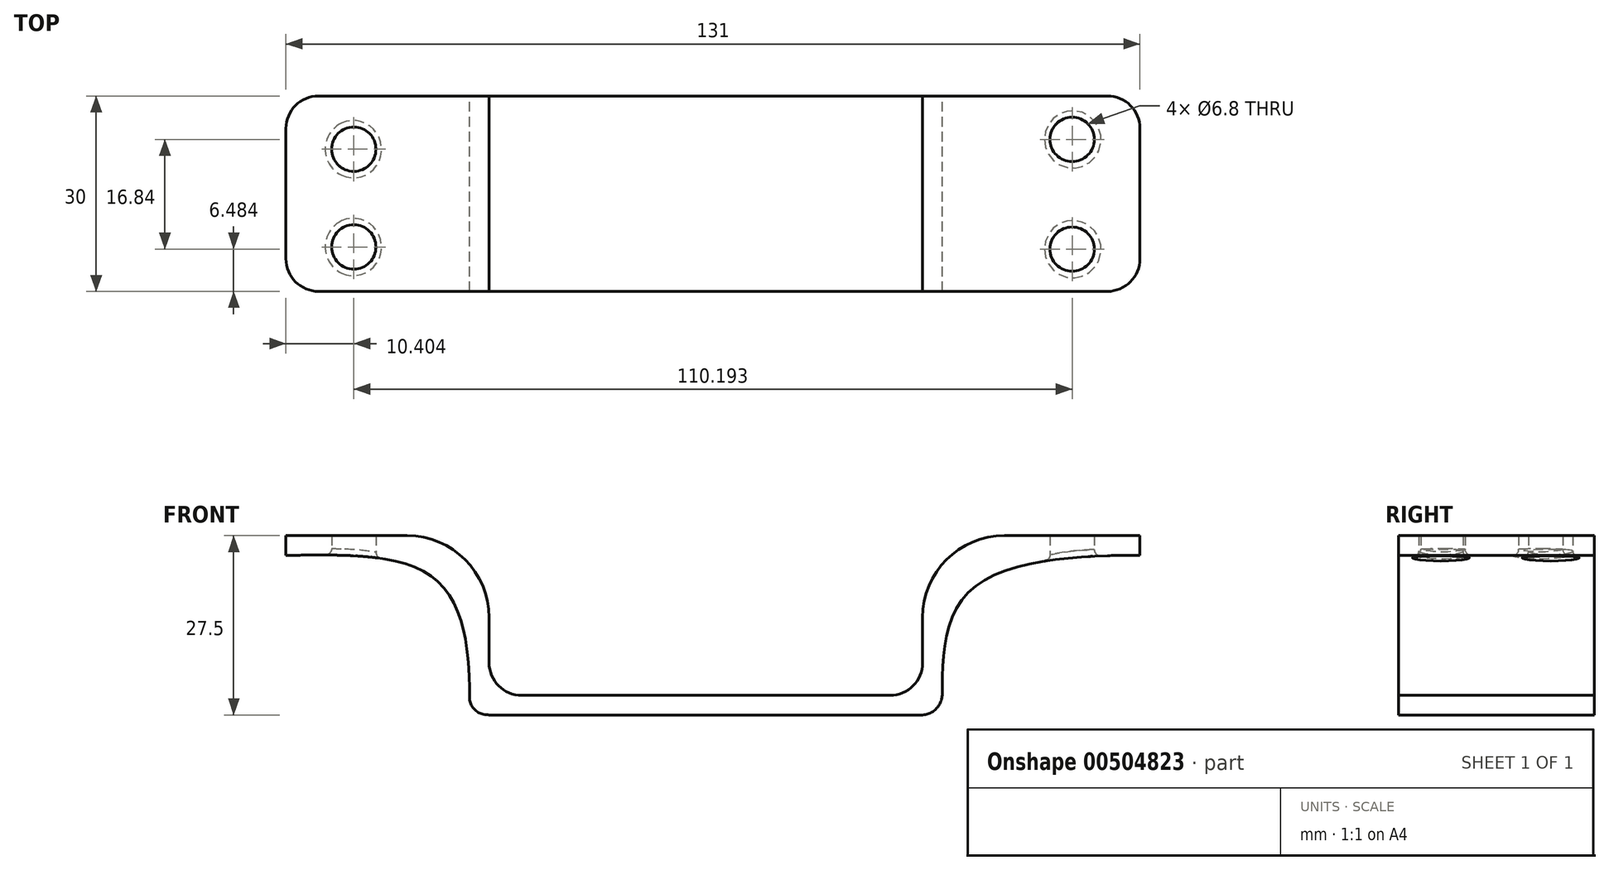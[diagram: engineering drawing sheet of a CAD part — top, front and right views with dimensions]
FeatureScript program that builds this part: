
annotation { "Feature Type Name" : "Feature", "Feature Type Description" : "" }
export const myFeature = defineFeature(function(context is Context, id is Id, definition is map)
    precondition{}
    {
        {
            var Q0;
            Q0=qCreatedBy(makeId("Front.planeOp"),FACE);
            var sketch = newSketch(context, id + "F0", { "sketchPlane" : qUnion([Q0])});
            skLineSegment(sketch, "E0.bottom", {"start": v(33.25, -1.5) * mm, "end": v(-33.25, -1.5) * mm});
            skLineSegment(sketch, "E0.top", {"start": v(33.25, 1.5) * mm, "end": v(-33.25, 1.5) * mm});
            skLineSegment(sketch, "E0.left", {"start": v(33.25, -1.5) * mm, "end": v(33.25, 1.5) * mm});
            skLineSegment(sketch, "E0.right", {"start": v(-33.25, -1.5) * mm, "end": v(-33.25, 1.5) * mm});
            skPoint(sketch, "E0.middle", {"position": v(0, 0) * mm});
            skLineSegment(sketch, "E1.bottom", {"start": v(33.25, 1.5) * mm, "end": v(36.25, 1.5) * mm});
            skLineSegment(sketch, "E1.top", {"start": v(33.25, 26) * mm, "end": v(36.25, 26) * mm});
            skLineSegment(sketch, "E1.left", {"start": v(33.25, 1.5) * mm, "end": v(33.25, 26) * mm});
            skLineSegment(sketch, "E1.right", {"start": v(36.25, 1.5) * mm, "end": v(36.25, 26) * mm});
            skLineSegment(sketch, "E2.bottom", {"start": v(-33.25, 1.5) * mm, "end": v(-36.25, 1.5) * mm});
            skLineSegment(sketch, "E2.top", {"start": v(-33.25, 26) * mm, "end": v(-36.25, 26) * mm});
            skLineSegment(sketch, "E2.left", {"start": v(-33.25, 1.5) * mm, "end": v(-33.25, 26) * mm});
            skLineSegment(sketch, "E2.right", {"start": v(-36.25, 1.5) * mm, "end": v(-36.25, 26) * mm});
            skLineSegment(sketch, "E3.bottom", {"start": v(-36.25, 26) * mm, "end": v(-64.4, 26) * mm});
            skLineSegment(sketch, "E3.top", {"start": v(-36.25, 23) * mm, "end": v(-64.4, 23) * mm});
            skLineSegment(sketch, "E3.left", {"start": v(-36.25, 26) * mm, "end": v(-36.25, 23) * mm});
            skLineSegment(sketch, "E3.right", {"start": v(-64.4, 26) * mm, "end": v(-64.4, 23) * mm});
            skLineSegment(sketch, "E4.bottom", {"start": v(36.25, 26) * mm, "end": v(66.59, 26) * mm});
            skLineSegment(sketch, "E4.top", {"start": v(36.25, 23) * mm, "end": v(66.59, 23) * mm});
            skLineSegment(sketch, "E4.left", {"start": v(36.25, 26) * mm, "end": v(36.25, 23) * mm});
            skLineSegment(sketch, "E4.right", {"start": v(66.59, 26) * mm, "end": v(66.59, 23) * mm});
            skFitSpline(sketch, "E5", {"points": [v(-64.4, 23) * mm, v(-41.43, 19.26) * mm, v(-36.25, 1.5) * mm], "startDerivative": vector(41.97, 0) * mm, "endDerivative": vector(0, -37.1) * mm});
            skFitSpline(sketch, "E6", {"points": [v(66.59, 23) * mm, v(40.74, 17.77) * mm, v(36.25, 1.5) * mm], "startDerivative": vector(-42.05, 0) * mm, "endDerivative": vector(0, -36.52) * mm});
            skFitSpline(sketch, "E7", {"points": [v(36.25, 1.5) * mm, v(33.25, -1.5) * mm], "startDerivative": vector(-0.1, -4.5) * mm, "endDerivative": vector(-4.89, -0.14) * mm});
            skFitSpline(sketch, "E8", {"points": [v(-36.25, 1.5) * mm, v(-33.25, -1.5) * mm], "startDerivative": vector(-0.2, -5.86) * mm, "endDerivative": vector(5.31, -0.02) * mm});
            skSolve(sketch);
        }
        {
            var Q0;
            Q0=makeQuery(id+"F0.imprint","IMPRINT",FACE,{"disambiguationData":[TD([[makeQuery(id+"F0.imprint","IMPRINT",EDGE,{"derivedFrom":sQuery(id+"F0.wireOp",EDGE,"E3.bottom")}),1.0]])]});
            var Q1;
            Q1=makeQuery(id+"F0.imprint","IMPRINT",FACE,{"disambiguationData":[TD([[makeQuery(id+"F0.imprint","IMPRINT",EDGE,{"derivedFrom":sQuery(id+"F0.wireOp",EDGE,"E2.right")}),1.0]])]});
            var Q2;
            Q2=makeQuery(id+"F0.imprint","IMPRINT",FACE,{"disambiguationData":[TD([[makeQuery(id+"F0.imprint","IMPRINT",EDGE,{"derivedFrom":sQuery(id+"F0.wireOp",EDGE,"E2.bottom")}),-1.0]])]});
            var Q3;
            Q3=makeQuery(id+"F0.imprint","IMPRINT",FACE,{"disambiguationData":[TD([[makeQuery(id+"F0.imprint","IMPRINT",EDGE,{"derivedFrom":sQuery(id+"F0.wireOp",EDGE,"E0.bottom")}),-1.0]])]});
            var Q4;
            Q4=makeQuery(id+"F0.imprint","IMPRINT",FACE,{"disambiguationData":[TD([[makeQuery(id+"F0.imprint","IMPRINT",EDGE,{"derivedFrom":sQuery(id+"F0.wireOp",EDGE,"E0.right")}),1.0]])]});
            var Q5;
            Q5=makeQuery(id+"F0.imprint","IMPRINT",FACE,{"disambiguationData":[TD([[makeQuery(id+"F0.imprint","IMPRINT",EDGE,{"derivedFrom":sQuery(id+"F0.wireOp",EDGE,"E1.right")}),-1.0]])]});
            var Q6;
            Q6=makeQuery(id+"F0.imprint","IMPRINT",FACE,{"disambiguationData":[TD([[makeQuery(id+"F0.imprint","IMPRINT",EDGE,{"derivedFrom":sQuery(id+"F0.wireOp",EDGE,"E4.bottom")}),-1.0]])]});
            var Q7;
            Q7=makeQuery(id+"F0.imprint","IMPRINT",FACE,{"disambiguationData":[TD([[makeQuery(id+"F0.imprint","IMPRINT",EDGE,{"derivedFrom":sQuery(id+"F0.wireOp",EDGE,"E1.bottom")}),1.0]])]});
            var Q8;
            Q8=makeQuery(id+"F0.imprint","IMPRINT",FACE,{"disambiguationData":[TD([[makeQuery(id+"F0.imprint","IMPRINT",EDGE,{"derivedFrom":sQuery(id+"F0.wireOp",EDGE,"E0.left")}),-1.0]])]});
            extrude(context, id + "F1", {"entities" : qUnion([Q0, Q1, Q2, Q3, Q4, Q5, Q6, Q7, Q8]), "endBound" : BoundingType.SYMMETRIC, "depth" : 30 * mm});
        }
        {
            var Q0;
            Q0=makeQuery(id+"F1.opExtrude","CAP_EDGE",EDGE,{"disambiguationData":[OSD([sQuery(id+"F0.wireOp",EDGE,"E4.right")])],"isStart":false});
            var Q1;
            Q1=makeQuery(id+"F1.opExtrude","CAP_EDGE",EDGE,{"disambiguationData":[OSD([sQuery(id+"F0.wireOp",EDGE,"E4.right")])],"isStart":true});
            var Q2;
            Q2=makeQuery(id+"F1.opExtrude","CAP_EDGE",EDGE,{"disambiguationData":[OSD([sQuery(id+"F0.wireOp",EDGE,"E3.right")])],"isStart":false});
            var Q3;
            Q3=makeQuery(id+"F1.opExtrude","CAP_EDGE",EDGE,{"disambiguationData":[OSD([sQuery(id+"F0.wireOp",EDGE,"E3.right")])],"isStart":true});
            fillet(context, id + "F2", {"entities" : qUnion([Q0, Q1, Q2, Q3]), "radius" : 5 * mm, "tangentPropagation" : true, "allowEdgeOverflow" : false});
        }
        {
            var Q0;
            Q0=makeQuery(id+"F1.opExtrude","SWEPT_EDGE",EDGE,{"disambiguationData":[OSD([sQuery(id+"F0.wireOp",EDGE,"E1.top"),sQuery(id+"F0.wireOp",EDGE,"E1.left")])]});
            var Q1;
            Q1=makeQuery(id+"F1.opExtrude","SWEPT_EDGE",EDGE,{"disambiguationData":[OSD([sQuery(id+"F0.wireOp",EDGE,"E2.top"),sQuery(id+"F0.wireOp",EDGE,"E2.left")])]});
            fillet(context, id + "F3", {"entities" : qUnion([Q0, Q1]), "radius" : 12.55 * mm, "tangentPropagation" : true, "allowEdgeOverflow" : false});
        }
        {
            var Q0;
            Q0=makeQuery(id+"F1.opExtrude","SWEPT_EDGE",EDGE,{"disambiguationData":[OSD([sQuery(id+"F0.wireOp",EDGE,"E0.top"),sQuery(id+"F0.wireOp",EDGE,"E0.left"),sQuery(id+"F0.wireOp",EDGE,"E1.bottom"),sQuery(id+"F0.wireOp",EDGE,"E1.left")])]});
            var Q1;
            Q1=makeQuery(id+"F1.opExtrude","SWEPT_EDGE",EDGE,{"disambiguationData":[OSD([sQuery(id+"F0.wireOp",EDGE,"E0.top"),sQuery(id+"F0.wireOp",EDGE,"E0.right"),sQuery(id+"F0.wireOp",EDGE,"E2.bottom"),sQuery(id+"F0.wireOp",EDGE,"E2.left")])]});
            fillet(context, id + "F4", {"entities" : qUnion([Q0, Q1]), "radius" : 5 * mm, "tangentPropagation" : true, "allowEdgeOverflow" : false});
        }
        {
            var Q0;
            Q0=qCreatedBy(makeId("Top.planeOp"),FACE);
            var sketch = newSketch(context, id + "F5", { "sketchPlane" : qUnion([Q0])});
            skCircle(sketch, "E9", {"center": v(-54, -8.18) * mm, "radius": 3.4 * mm});
            skCircle(sketch, "E10", {"center": v(-54, 6.82) * mm, "radius": 3.4 * mm});
            skCircle(sketch, "E11", {"center": v(56.19, -8.52) * mm, "radius": 3.4 * mm});
            skCircle(sketch, "E12", {"center": v(56.19, 8.32) * mm, "radius": 3.4 * mm});
            skSolve(sketch);
        }
        {
            var Q0;
            Q0=makeQuery(id+"F5.imprint","IMPRINT",FACE,{"disambiguationData":[TD([[makeQuery(id+"F5.imprint","IMPRINT",EDGE,{"derivedFrom":sQuery(id+"F5.wireOp",EDGE,"E9")}),1.0]])]});
            var Q1;
            Q1=makeQuery(id+"F5.imprint","IMPRINT",FACE,{"disambiguationData":[TD([[makeQuery(id+"F5.imprint","IMPRINT",EDGE,{"derivedFrom":sQuery(id+"F5.wireOp",EDGE,"E10")}),1.0]])]});
            var Q2;
            Q2=makeQuery(id+"F5.imprint","IMPRINT",FACE,{"disambiguationData":[TD([[makeQuery(id+"F5.imprint","IMPRINT",EDGE,{"derivedFrom":sQuery(id+"F5.wireOp",EDGE,"E11")}),1.0]])]});
            var Q3;
            Q3=makeQuery(id+"F5.imprint","IMPRINT",FACE,{"disambiguationData":[TD([[makeQuery(id+"F5.imprint","IMPRINT",EDGE,{"derivedFrom":sQuery(id+"F5.wireOp",EDGE,"E12")}),1.0]])]});
            extrude(context, id + "F6", {"entities" : qUnion([Q0, Q1, Q2, Q3]), "operationType" : NewBodyOperationType.REMOVE, "depth" : 57.1 * mm});
        }
        {
            var Q0;
            Q0=makeQuery(id+"F6.boolean.opBoolean","INTERSECT",EDGE,{"derivedFrom":[makeQuery(id+"F1.opExtrude","SWEPT_FACE",FACE,{"disambiguationData":[OSD([sQuery(id+"F0.wireOp",EDGE,"E5")])]}),makeQuery(id+"F6.opExtrude","SWEPT_FACE",FACE,{"disambiguationData":[OSD([sQuery(id+"F5.wireOp",EDGE,"E9")])]})]});
            var Q1;
            Q1=makeQuery(id+"F6.boolean.opBoolean","INTERSECT",EDGE,{"derivedFrom":[makeQuery(id+"F1.opExtrude","SWEPT_FACE",FACE,{"disambiguationData":[OSD([sQuery(id+"F0.wireOp",EDGE,"E5")])]}),makeQuery(id+"F6.opExtrude","SWEPT_FACE",FACE,{"disambiguationData":[OSD([sQuery(id+"F5.wireOp",EDGE,"E10")])]})]});
            var Q2;
            Q2=makeQuery(id+"F6.boolean.opBoolean","INTERSECT",EDGE,{"derivedFrom":[makeQuery(id+"F1.opExtrude","SWEPT_FACE",FACE,{"disambiguationData":[OSD([sQuery(id+"F0.wireOp",EDGE,"E6")])]}),makeQuery(id+"F6.opExtrude","SWEPT_FACE",FACE,{"disambiguationData":[OSD([sQuery(id+"F5.wireOp",EDGE,"E11")])]})]});
            var Q3;
            Q3=makeQuery(id+"F6.boolean.opBoolean","INTERSECT",EDGE,{"derivedFrom":[makeQuery(id+"F1.opExtrude","SWEPT_FACE",FACE,{"disambiguationData":[OSD([sQuery(id+"F0.wireOp",EDGE,"E6")])]}),makeQuery(id+"F6.opExtrude","SWEPT_FACE",FACE,{"disambiguationData":[OSD([sQuery(id+"F5.wireOp",EDGE,"E12")])]})]});
            fillet(context, id + "F7", {"entities" : qUnion([Q0, Q1, Q2, Q3]), "radius" : 1 * mm, "tangentPropagation" : true, "allowEdgeOverflow" : false});
        }
    });
